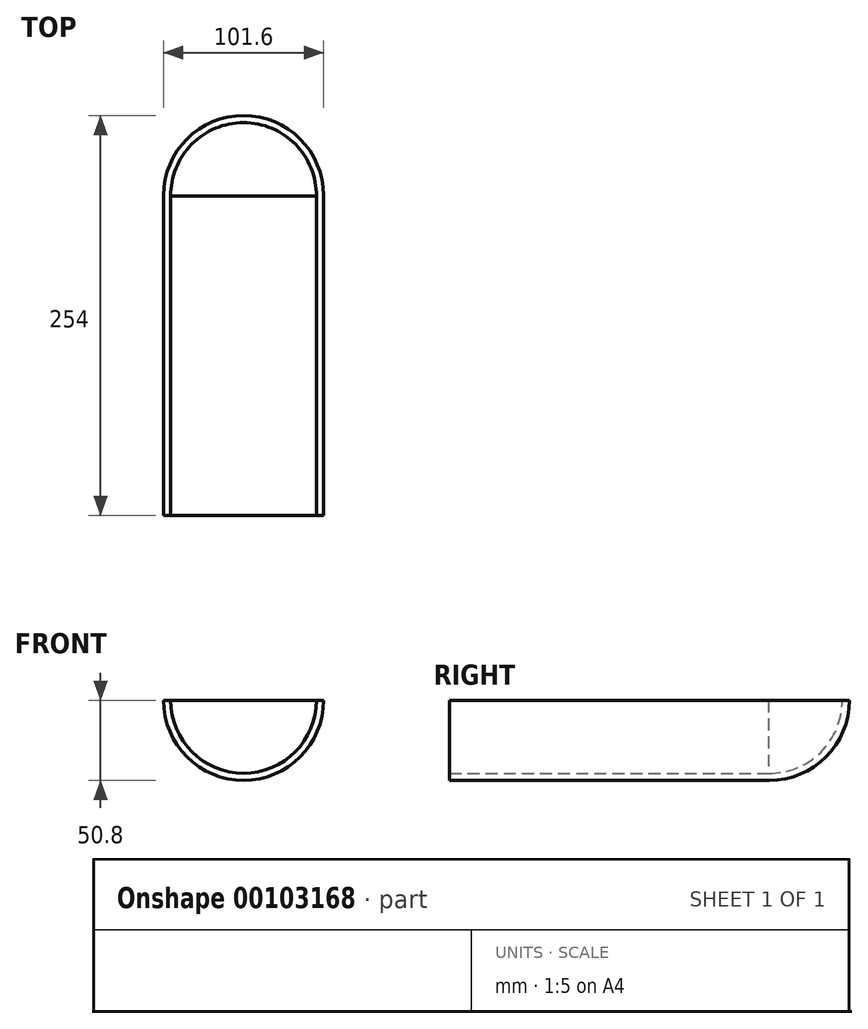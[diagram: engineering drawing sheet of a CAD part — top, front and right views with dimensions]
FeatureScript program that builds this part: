
annotation { "Feature Type Name" : "Feature", "Feature Type Description" : "" }
export const myFeature = defineFeature(function(context is Context, id is Id, definition is map)
    precondition{}
    {
        {
            var Q0;
            Q0=qCreatedBy(makeId("Top.planeOp"),FACE);
            var sketch = newSketch(context, id + "F0", { "sketchPlane" : qUnion([Q0])});
            skLineSegment(sketch, "E0.bottom", {"start": v(0, -101.6) * mm, "end": v(-50.8, -101.6) * mm});
            skLineSegment(sketch, "E0.right", {"start": v(-50.8, -101.6) * mm, "end": v(-50.8, 101.6) * mm});
            skPoint(sketch, "E0.middle", {"position": v(0, 0) * mm});
            skPoint(sketch, "E0.left.start.orphan", {"position": v(50.8, -101.6) * mm});
            skPoint(sketch, "E1.orphan", {"position": v(50.8, 101.6) * mm});
            skLineSegment(sketch, "E2", {"start": v(0, 147.9) * mm, "end": v(0, 152.4) * mm});
            skArc(sketch, "E3.trimOffspring", {"start": v(0, 152.4) * mm, "mid": v(-35.92, 137.52) * mm, "end": v(-50.8, 101.6) * mm});
            skLineSegment(sketch, "E4", {"start": v(-46.29, -101.6) * mm, "end": v(-46.29, 102.1) * mm});
            skArc(sketch, "E5", {"start": v(0, 147.9) * mm, "mid": v(-32.9, 134.16) * mm, "end": v(-46.29, 101.1) * mm});
            skLineSegment(sketch, "E6", {"start": v(0, 101.6) * mm, "end": v(0, -101.6) * mm});
            skSolve(sketch);
        }
        {
            var Q0;
            {var subQ1=sQuery(id+"F0.wireOp",EDGE,"E0.right");Q0=makeQuery(id+"F0.imprint","IMPRINT",FACE,{"disambiguationData":[TD([[makeQuery(id+"F0.imprint","IMPRINT",EDGE,{"derivedFrom":subQ1}),-1.0]])]});}
            var Q1;
            Q1=sQuery(id+"F0.wireOp",EDGE,"E6");
            revolve(context, id + "F1", {"entities" : qUnion([Q0]), "axis" : qUnion([Q1]), "revolveType" : RevolveType.ONE_DIRECTION, "angle" : 180 * degree});
        }
    });
